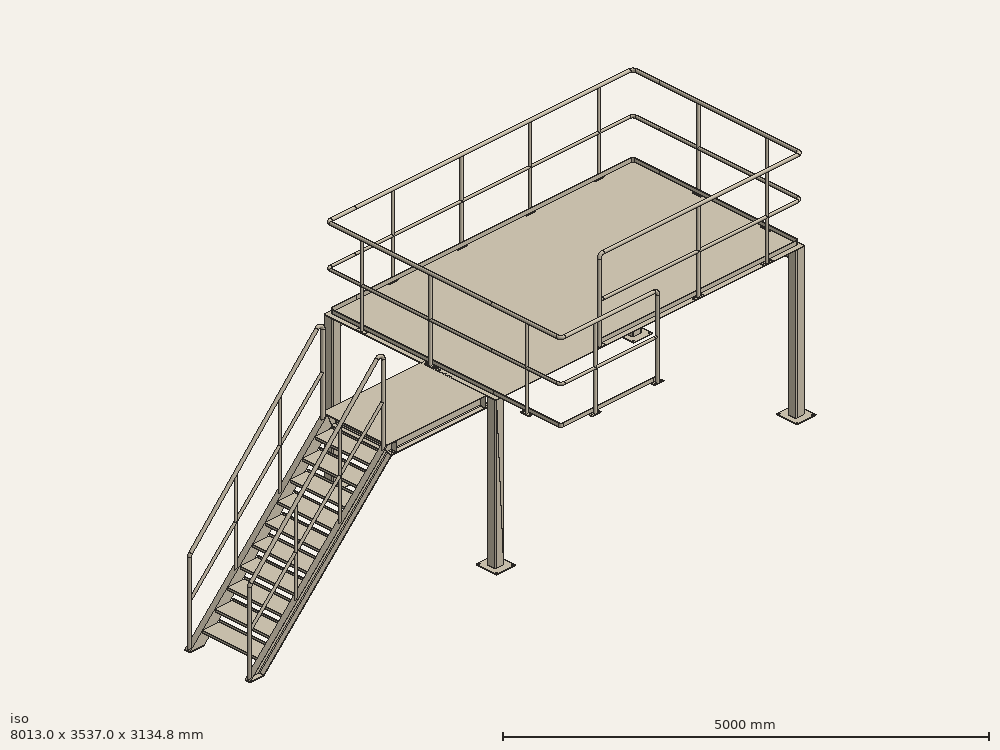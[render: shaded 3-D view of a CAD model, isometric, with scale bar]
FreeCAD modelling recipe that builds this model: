
FCSTD DOCUMENT  (FreeCAD 1.0R39319 (Git))
Label: trestle01
License: All rights reserved
objects: Part::FeaturePython×11, App::Part×4, Sketcher::SketchObject×2, Part::Feature×2, Spreadsheet::Sheet×1, Part::Extrusion×1, PartDesign::Pad×1
note: 21 computed .brp shape members not serialized (recipe doc carries the construction recipe); baked Part::Feature solids carry a one-line shape summary decoded from their .brp

FEATURE [Spreadsheet::Sheet] Spreadsheet
  cells = A1(key)='01; A2='W; B2(W0)=4500; A3='L; B3(L0)=2500; A4='H; B4(H0)=2000; A5='y1; B5(y1)=75; A6='y2; B6(y2)=950
FEATURE [Sketcher::SketchObject] Sketch
  ArcFitTolerance = 0
  FullyConstrained = true
  MakeInternals = false
  expr: Constraints[8] = Spreadsheet.L0
  expr: Constraints[9] = Spreadsheet.W0
  sketch-geometry (4):
    g0: LineSegment StartX=-62.5 StartY=-62.5 StartZ=0 EndX=4437.5 EndY=-62.5 EndZ=0
    g1: LineSegment StartX=4437.5 StartY=-62.5 StartZ=0 EndX=4437.5 EndY=2437.5 EndZ=0
    g2: LineSegment StartX=4437.5 StartY=2437.5 StartZ=0 EndX=-62.5 EndY=2437.5 EndZ=0
    g3: LineSegment StartX=-62.5 StartY=2437.5 StartZ=0 EndX=-62.5 EndY=-62.5 EndZ=0
  constraints (12):
    c: Coincident(g0,g1)
    c: Coincident(g1,g2)
    c: Coincident(g2,g3)
    c: Coincident(g3,g0)
    c: Horizontal(g0)
    c: Horizontal(g2)
    c: Vertical(g1)
    c: Vertical(g3)
    c: DistanceY(g3,g3) = 2500
    c: DistanceX(g2,g2) = 4500
    c: DistanceY(g0,g-1) = 62.5
    c: DistanceX(g0,g-1) = 62.5
FEATURE [Part::Extrusion] Extrude001  label="chpl"
  Base = -> Sketch
  Dir = (0,0,1)
  DirMode = 2
  FaceMakerClass = Part::FaceMakerBullseye
  FaceMakerMode = 3
  LengthFwd = 4.5
  LengthRev = 0
  Placement = pos=(0,0,2000) rot=(0,0,1;0rad)
  Solid = true
  Symmetric = false
  expr: .Placement.Base.z = Spreadsheet.H0
FEATURE [Part::FeaturePython] Corner_with_end  # WARN: FeaturePython — macro-defined, semantics opaque (R4)
  Placement = pos=(1373,-987,2004.5) rot=(0,0,1;3.14159rad)
  Reverse = true
  Standard = L1=1410.0,L2=1000.0
  g0 = 7.85
  h = 1100
  k = -90
  l1 = 1410
  l2 = 1000
  mass = 29.375
  p = 1000
  spec = 0
  type = 1
  expr: .Placement.Base.z = Spreadsheet.H0 + 4.5
FEATURE [Part::FeaturePython] Corner  # WARN: FeaturePython — macro-defined, semantics opaque (R4)
  Placement = pos=(-37,13,2004.5) rot=(0,0,1;1.5708rad)
  Reverse = true
  Standard = L1=2400.0,L2=400.0
  g0 = 7.85
  h = 1100
  k = -90
  l1 = 2400
  l2 = 400
  mass = 28.4497
  p = 1000
  spec = 0
  type = 2
  expr: .Placement.Base.z = Spreadsheet.H0 + 4.5
  expr: l1 = Spreadsheet.L0 - 100
FEATURE [Part::FeaturePython] Corner001  # WARN: FeaturePython — macro-defined, semantics opaque (R4)
  Placement = pos=(363,2413,2004.5) rot=(0,0,1;0rad)
  Reverse = true
  Standard = L1=4050.0,L2=400.0
  g0 = 7.85
  h = 1100
  k = -90
  l1 = 4050
  l2 = 400
  mass = 47.7545
  p = 1000
  spec = 0
  type = 2
  expr: .Placement.Base.y = Spreadsheet.L0 - 87
  expr: .Placement.Base.z = Spreadsheet.H0 + 4.5
  expr: l1 = Spreadsheet.W0 - 450
FEATURE [Part::FeaturePython] Corner_with_end001  # WARN: FeaturePython — macro-defined, semantics opaque (R4)
  Placement = pos=(1473,-37,2004.5) rot=(0,0,1;0rad)
  Reverse = false
  Standard = L1=2940.0,L2=2050.0
  g0 = 7.85
  h = 1100
  k = 90
  l1 = 2940
  l2 = 2050
  mass = 56.2785
  p = 1000
  spec = 0
  type = 1
  expr: .Placement.Base.z = Spreadsheet.H0 + 4.5
  expr: l1 = Spreadsheet.W0 - 1560
  expr: l2 = Spreadsheet.L0 - 450
FEATURE [Sketcher::SketchObject] Sketch001
  ArcFitTolerance = 1e-06
  FullyConstrained = true
  MakeInternals = false
  MapMode = 5
  Placement = pos=(0,0,0) rot=(1,0,0;3.14159rad)
  sketch-geometry (9):
    g0: LineSegment StartX=-138 StartY=-150 StartZ=0 EndX=138 EndY=-150 EndZ=0
    g1: LineSegment StartX=138 StartY=-150 StartZ=0 EndX=138 EndY=150 EndZ=0
    g2: LineSegment StartX=138 StartY=150 StartZ=0 EndX=-138 EndY=150 EndZ=0
    g3: LineSegment StartX=-138 StartY=150 StartZ=0 EndX=-138 EndY=-150 EndZ=0
    g4: GeomPoint [constr] X=-2e-16 Y=3e-16 Z=0
    g5: Circle CenterX=-113 CenterY=125 CenterZ=0 NormalX=0 NormalY=0 NormalZ=1 AngleXU=0 Radius=10
    g6: Circle CenterX=-113 CenterY=-125 CenterZ=0 NormalX=0 NormalY=0 NormalZ=1 AngleXU=0 Radius=10
    g7: Circle CenterX=113 CenterY=-125 CenterZ=0 NormalX=0 NormalY=0 NormalZ=1 AngleXU=0 Radius=10
    g8: Circle CenterX=113 CenterY=125 CenterZ=0 NormalX=0 NormalY=0 NormalZ=1 AngleXU=0 Radius=10
  constraints (24):
    c: Coincident(g0,g1)
    c: Coincident(g1,g2)
    c: Coincident(g2,g3)
    c: Coincident(g3,g0)
    c: Horizontal(g0)
    c: Horizontal(g2)
    c: Vertical(g1)
    c: Vertical(g3)
    c: Symmetric(g2,g0,g4)
    c: Coincident(g4,g-1)
    c: DistanceY(g-3,g1) = 50
    c: DistanceX(g-5,g0) = 50
    c: Diameter(g5) = 20
    c: Equal(g5,g6)
    c: Equal(g6,g7)
    c: Equal(g7,g8)
    c: Vertical(g5,g6)
    c: Vertical(g8,g7)
    c: Horizontal(g5,g8)
    c: Horizontal(g6,g7)
    c: DistanceY(g5,g2) = 25
    c: DistanceX(g2,g5) = 25
    c: DistanceX(g8,g1) = 25
    c: DistanceY(g0,g7) = 25
FEATURE [PartDesign::Pad] Pad  label="plt"
  Direction = (0,-1e-16,-1)
  Length = 9
  Length2 = 10
  Placement = pos=(0,0,0) rot=(1,0,0;3.14159rad)
  Profile = -> Sketch001
  ReferenceAxis = -> Sketch001 [N_Axis]
  Refine = true
  Suppressed = false
  Type = 0
FEATURE [Part::FeaturePython] SquarePipe  # WARN: FeaturePython — macro-defined, semantics opaque (R4)
  A = 125
  B = 125
  JPN = 角形鋼管
  L = 2000
  Placement = pos=(0,0,0) rot=(1,0,0;1.5708rad)
  Solid = true
  Standard = L=2000
  g0 = 7.85
  mass = 43.3837
  size = 40
  standard = SS
  t = 6
  type = 10_Square_Pipe
  expr: L = Spreadsheet.H0
FEATURE [App::Part] Part001  label="pst_SQ"
  Group = -> [Pad,Sketch001,SquarePipe]
  JPN = 支柱
  Origin = -> Origin001
  Standard = □125x125x6 , H=2200
  count = 1
  g0 = 7.85
  mass = 84.5691
  material = SS41
FEATURE [Part::FeaturePython] Array  # Draft array (typed FeaturePython)
  Angle = 360
  ArrayType = 0
  Axis = (0,0,1)
  Base = -> Part001
  Center = (0,0,0)
  Count = 4
  Fuse = true
  IntervalAxis = (0,0,0)
  IntervalX = (4375,0,0)
  IntervalY = (0,2375,0)
  IntervalZ = (0,0,100)
  NumberCircles = 3
  NumberPolar = 5
  NumberX = 2
  NumberY = 2
  NumberZ = 1
  RadialDistance = 50
  Symmetry = 1
  TangentialDistance = 25
  expr: .IntervalX.x = Spreadsheet.W0 - 125
  expr: .IntervalY.y = Spreadsheet.L0 - 125
FEATURE [Part::FeaturePython] ChannelSteel  # WARN: FeaturePython — macro-defined, semantics opaque (R4)
  B = 75
  H = 150
  JPN = 溝形鋼
  L = 2250
  Placement = pos=(0,67.5,1925) rot=(0,1,0;3.14159rad)
  Solid = true
  Standard = L=2250
  g0 = 7.85
  mass = 33.8098
  size = 3
  standard = SS
  t1 = 6.5
  t2 = 10
  type = 01_Channel
  expr: .Placement.Base.z = Spreadsheet.H0 - 75
  expr: L = Spreadsheet.L0 - 250
FEATURE [Part::FeaturePython] Clone  label="ChannelSteel001"  # Draft clone (typed FeaturePython)
  AttacherType = Attacher::AttachEngine3D
  Fuse = false
  Objects = -> [ChannelSteel]
  Placement = pos=(4375,67.5,1925) rot=(0,0,1;0rad)
  Scale = (1,1,1)
  expr: .Placement.Base.x = Spreadsheet.W0 - 125
  expr: .Placement.Base.z = Spreadsheet.H0 - 75
FEATURE [Part::FeaturePython] ChannelSteel001  label="ChannelSteel002"  # WARN: FeaturePython — macro-defined, semantics opaque (R4)
  B = 75
  H = 150
  JPN = 溝形鋼
  L = 4250
  Placement = pos=(62.5,0,1925) rot=(0,0,1;4.71239rad)
  Solid = true
  Standard = L=4250
  g0 = 7.85
  mass = 92.9768
  size = 3
  standard = SS
  t1 = 6.5
  t2 = 10
  type = 01_Channel
  expr: .Placement.Base.z = Spreadsheet.H0 - 75
  expr: L = Spreadsheet.W0 - 250
FEATURE [Part::FeaturePython] Clone001  label="ChannelSteel003"  # Draft clone (typed FeaturePython)
  AttacherType = Attacher::AttachEngine3D
  Fuse = false
  Objects = -> [ChannelSteel001]
  Placement = pos=(62.5,2375,1925) rot=(-0.707107,-0.707107,0;3.14159rad)
  Scale = (1,1,1)
  expr: .Placement.Base.y = Spreadsheet.L0 - 125
  expr: .Placement.Base.z = Spreadsheet.H0 - 75
FEATURE [App::Part] Part  label="Trstle01"
  Group = -> [Sketch,Extrude001,Corner_with_end,Corner,Corner001,Corner_with_end001,Part001,Array,ChannelSteel,Clone,ChannelSteel001,Clone001]
  Origin = -> Origin
FEATURE [Part::FeaturePython] stair  # WARN: FeaturePython — macro-defined, semantics opaque (R4)
  ClockWise = true
  H0 = 2000
  JPN = 鋼製階段
  L = 2000
  L1 = 1500
  MdlFloor = false
  Placement = pos=(-3500,950,0) rot=(0,0,1;0rad)
  Rail = 0
  Standard = L=2000.0
  body = 284.113
  handrail = 54.2281
  mass = 338.342
  size = 1
  story = 2
  t = 9
  t0 = 0
  type = 1
  w0 = 800
  w1 = 950
  w2 = 0
  w3 = 0
  expr: .Placement.Base.x = -(Spreadsheet.H0 + 1500)
  expr: H0 = Spreadsheet.H0
  expr: L = Spreadsheet.H0
FEATURE [Part::Feature] stair_Handrail_0_0
  Placement = pos=(-3470,75,30) rot=(0,0,1;0rad)
  shape: bbox 1994 x 42.7 x 3093 mm, 16 faces (baked)
  expr: .Placement.Base.x = -(Spreadsheet.H0 + 1500 - 30)
  expr: .Placement.Base.y = Spreadsheet.y1
FEATURE [Part::Feature] stair_Handrail_0_1
  Placement = pos=(-3470,950,30) rot=(0,0,1;0rad)
  shape: bbox 1994 x 42.7 x 3093 mm, 16 faces (baked)
  expr: .Placement.Base.x = -(Spreadsheet.H0 + 1500 - 30)
  expr: .Placement.Base.y = Spreadsheet.y2
FEATURE [App::Part] stair_Assy  label="stair001"
  Group = -> [stair,stair_Handrail_0_0,stair_Handrail_0_1]
  Origin = -> Origin002
  Placement = pos=(0,0,0) rot=(0,0,1;3.14159rad)
FEATURE [App::Part] Part002  label="trestleAssy"
  Group = -> [Spreadsheet,stair_Assy,Part]
  Origin = -> Origin003
